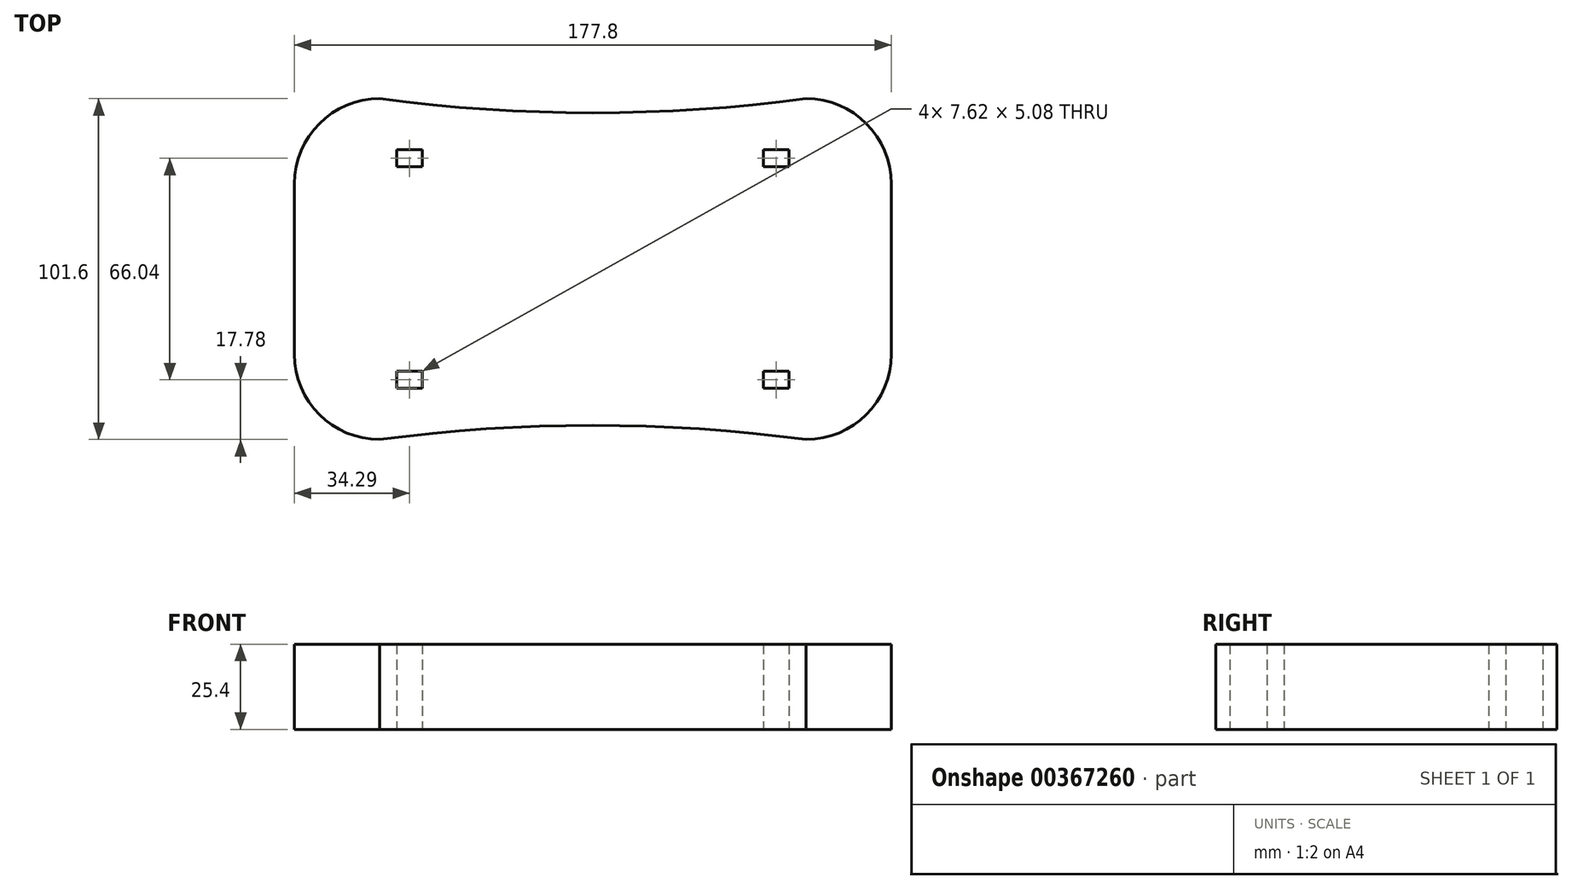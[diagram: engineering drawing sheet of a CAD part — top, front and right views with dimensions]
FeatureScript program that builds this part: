
annotation { "Feature Type Name" : "Feature", "Feature Type Description" : "" }
export const myFeature = defineFeature(function(context is Context, id is Id, definition is map)
    precondition{}
    {
        {
            var Q0;
            Q0=qCreatedBy(makeId("Top.planeOp"),FACE);
            var sketch = newSketch(context, id + "F0", { "sketchPlane" : qUnion([Q0])});
            skLineSegment(sketch, "E0.rect.left", {"start": v(88.9, -25.4) * mm, "end": v(88.9, 25.4) * mm});
            skLineSegment(sketch, "E0.rect.right", {"start": v(-88.9, -25.4) * mm, "end": v(-88.9, 25.4) * mm});
            skPoint(sketch, "E0.rect.middle", {"position": v(0, 0) * mm});
            skPoint(sketch, "E1.visualSharp", {"position": v(-88.9, 50.8) * mm});
            skArc(sketch, "E1.filletArc", {"start": v(-63.5, 50.8) * mm, "mid": v(-81.46, 43.36) * mm, "end": v(-88.9, 25.4) * mm});
            skPoint(sketch, "E2.visualSharp", {"position": v(-88.9, -50.8) * mm});
            skArc(sketch, "E2.filletArc", {"start": v(-88.9, -25.4) * mm, "mid": v(-81.46, -43.36) * mm, "end": v(-63.5, -50.8) * mm});
            skPoint(sketch, "E3.visualSharp", {"position": v(88.9, -50.8) * mm});
            skArc(sketch, "E3.filletArc", {"start": v(63.5, -50.8) * mm, "mid": v(81.46, -43.36) * mm, "end": v(88.9, -25.4) * mm});
            skPoint(sketch, "E4.visualSharp", {"position": v(88.9, 50.8) * mm});
            skArc(sketch, "E4.filletArc", {"start": v(88.9, 25.4) * mm, "mid": v(81.46, 43.36) * mm, "end": v(63.5, 50.8) * mm});
            skArc(sketch, "E5", {"start": v(-63.5, 50.8) * mm, "mid": v(0, 46.58) * mm, "end": v(63.5, 50.8) * mm});
            skPoint(sketch, "E5.third.point", {"position": v(0, 46.58) * mm});
            skArc(sketch, "E6.MirrorCS", {"start": v(-63.5, -50.8) * mm, "mid": v(0, -46.58) * mm, "end": v(63.5, -50.8) * mm});
            skLineSegment(sketch, "E7.bottom", {"start": v(-58.42, 35.56) * mm, "end": v(-50.8, 35.56) * mm});
            skLineSegment(sketch, "E7.top", {"start": v(-58.42, 30.48) * mm, "end": v(-50.8, 30.48) * mm});
            skLineSegment(sketch, "E7.left", {"start": v(-58.42, 35.56) * mm, "end": v(-58.42, 30.48) * mm});
            skLineSegment(sketch, "E7.right", {"start": v(-50.8, 35.56) * mm, "end": v(-50.8, 30.48) * mm});
            skLineSegment(sketch, "E8.MirrorCS", {"start": v(-50.8, -35.56) * mm, "end": v(-50.8, -30.48) * mm});
            skLineSegment(sketch, "E9.MirrorCS", {"start": v(-58.42, -35.56) * mm, "end": v(-58.42, -30.48) * mm});
            skLineSegment(sketch, "E10.MirrorCS", {"start": v(-58.42, -30.48) * mm, "end": v(-50.8, -30.48) * mm});
            skLineSegment(sketch, "E11.MirrorCS", {"start": v(-58.42, -35.56) * mm, "end": v(-50.8, -35.56) * mm});
            skLineSegment(sketch, "E12.MirrorCS", {"start": v(50.8, -35.56) * mm, "end": v(50.8, -30.48) * mm});
            skLineSegment(sketch, "E13.MirrorCS", {"start": v(50.8, 35.56) * mm, "end": v(50.8, 30.48) * mm});
            skLineSegment(sketch, "E14.MirrorCS", {"start": v(58.42, 35.56) * mm, "end": v(58.42, 30.48) * mm});
            skLineSegment(sketch, "E15.MirrorCS", {"start": v(58.42, -35.56) * mm, "end": v(58.42, -30.48) * mm});
            skLineSegment(sketch, "E16.MirrorCS", {"start": v(58.42, 30.48) * mm, "end": v(50.8, 30.48) * mm});
            skLineSegment(sketch, "E17.MirrorCS", {"start": v(58.42, -30.48) * mm, "end": v(50.8, -30.48) * mm});
            skLineSegment(sketch, "E18.MirrorCS", {"start": v(58.42, 35.56) * mm, "end": v(50.8, 35.56) * mm});
            skLineSegment(sketch, "E19.MirrorCS", {"start": v(58.42, -35.56) * mm, "end": v(50.8, -35.56) * mm});
            skSolve(sketch);
        }
        {
            var Q0;
            Q0=qSketchRegion(id+"F0",true);
            extrude(context, id + "F1", {"entities" : qUnion([Q0]), "depth" : 25.4 * mm});
        }
    });
